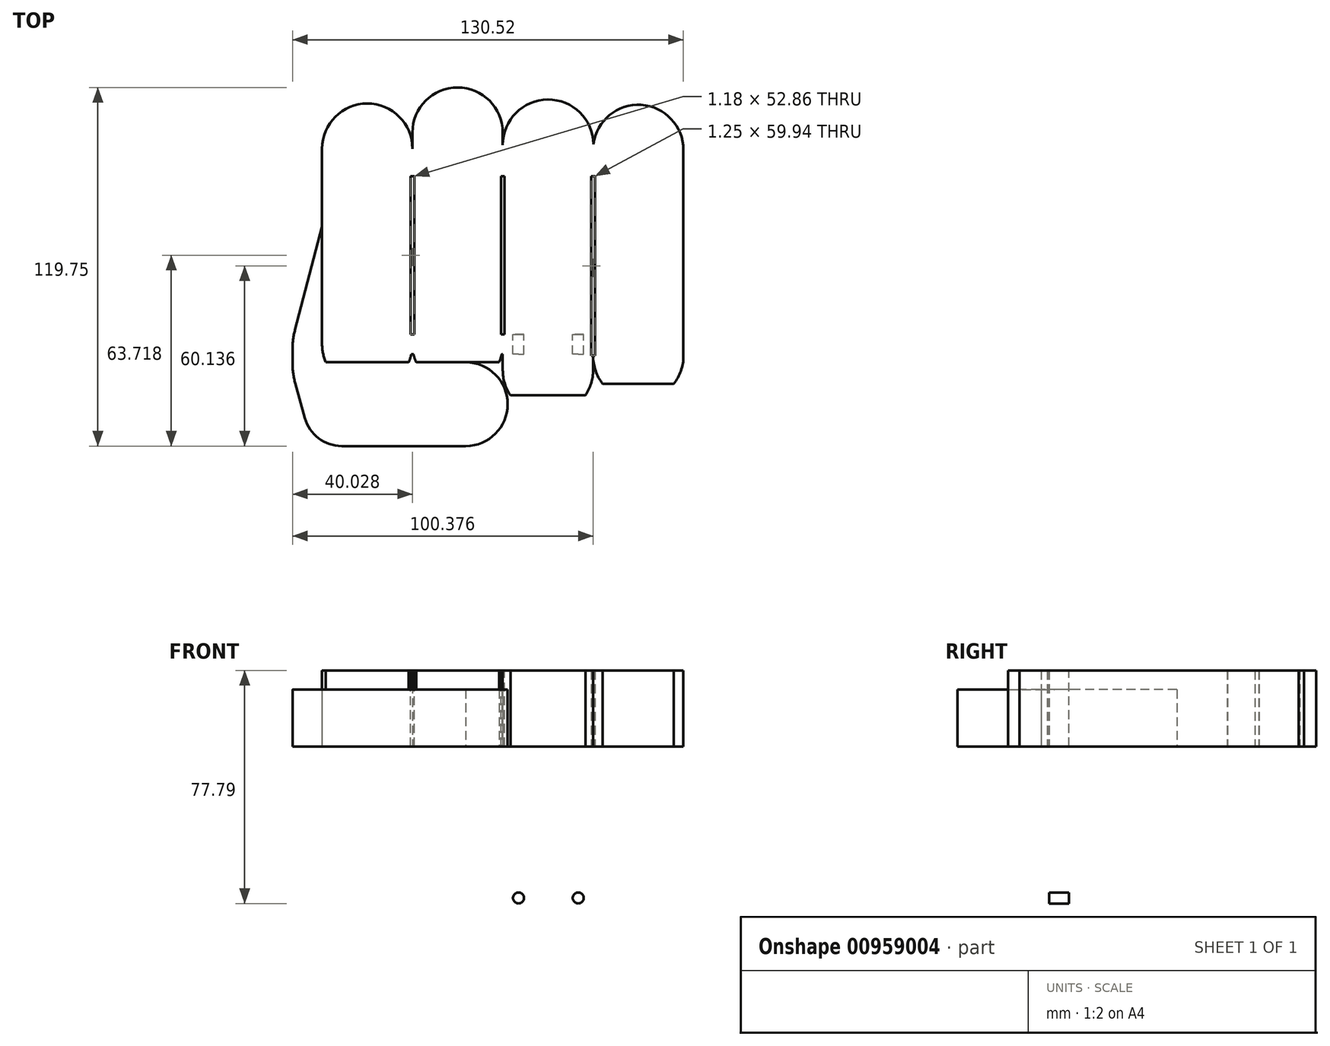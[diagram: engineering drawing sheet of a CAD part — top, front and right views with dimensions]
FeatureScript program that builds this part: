
annotation { "Feature Type Name" : "Feature", "Feature Type Description" : "" }
export const myFeature = defineFeature(function(context is Context, id is Id, definition is map)
    precondition{}
    {
        {
            var Q0;
            Q0=qCreatedBy(makeId("Top.planeOp"),FACE);
            var sketch = newSketch(context, id + "F0", { "sketchPlane" : qUnion([Q0])});
            skPoint(sketch, "E0.middle", {"position": v(0, 0) * mm});
            skArc(sketch, "E1", {"start": v(-30.16, -39.29) * mm, "mid": v(-29.85, -42.36) * mm, "end": v(-28.91, -45.3) * mm});
            skArc(sketch, "E2", {"start": v(0, -47.92) * mm, "mid": v(0.66, -52.32) * mm, "end": v(2.57, -56.34) * mm});
            skArc(sketch, "E3", {"start": v(-60.32, -39.28) * mm, "mid": v(-60, -42.35) * mm, "end": v(-59.07, -45.3) * mm});
            skArc(sketch, "E4", {"start": v(30.17, -43.19) * mm, "mid": v(31, -48.13) * mm, "end": v(33.4, -52.53) * mm});
            skLineSegment(sketch, "E5", {"start": v(-59.07, -45.3) * mm, "end": v(-31.41, -45.3) * mm});
            skArc(sketch, "E6.trimOffspring", {"start": v(-31.41, -45.3) * mm, "mid": v(-30.48, -42.36) * mm, "end": v(-30.16, -39.29) * mm});
            skArc(sketch, "E7.trimOffspring", {"start": v(-1.25, -45.3) * mm, "mid": v(-0.32, -42.36) * mm, "end": v(0, -39.29) * mm});
            skLineSegment(sketch, "E8.trimOffspring", {"start": v(-28.91, -45.3) * mm, "end": v(-1.25, -45.3) * mm});
            skArc(sketch, "E9", {"start": v(-12.33, -73.25) * mm, "mid": v(1.64, -59.27) * mm, "end": v(-12.33, -45.3) * mm});
            skLineSegment(sketch, "E10", {"start": v(-63.46, -73.25) * mm, "end": v(-12.33, -73.25) * mm});
            skLineSegment(sketch, "E11", {"start": v(33.4, -52.53) * mm, "end": v(57.09, -52.53) * mm});
            skArc(sketch, "E12.trimOffspring", {"start": v(27.6, -56.34) * mm, "mid": v(29.5, -52.32) * mm, "end": v(30.16, -47.92) * mm});
            skArc(sketch, "E13.trimOffspring", {"start": v(57.09, -52.53) * mm, "mid": v(59.5, -48.13) * mm, "end": v(60.33, -43.19) * mm});
            skArc(sketch, "E14", {"start": v(-30.16, 26.05) * mm, "mid": v(-45.24, 41.14) * mm, "end": v(-60.32, 26.05) * mm});
            skArc(sketch, "E15", {"start": v(0, 31.42) * mm, "mid": v(-15.08, 46.5) * mm, "end": v(-30.16, 31.42) * mm});
            skArc(sketch, "E16", {"start": v(60.33, 25.64) * mm, "mid": v(46.2, 40.7) * mm, "end": v(30.29, 27.55) * mm});
            skLineSegment(sketch, "E17", {"start": v(-60.32, 26.05) * mm, "end": v(-60.32, -39.28) * mm});
            skLineSegment(sketch, "E18", {"start": v(-30.16, 31.42) * mm, "end": v(-30.16, 26.05) * mm});
            skLineSegment(sketch, "E19", {"start": v(0, 31.42) * mm, "end": v(0, 27.33) * mm});
            skLineSegment(sketch, "E20", {"start": v(60.33, -43.19) * mm, "end": v(60.33, 25.64) * mm});
            skLineSegment(sketch, "E21", {"start": v(2.57, -56.34) * mm, "end": v(27.6, -56.34) * mm});
            skArc(sketch, "E22", {"start": v(30.29, 27.55) * mm, "mid": v(15.04, 42.47) * mm, "end": v(0, 27.33) * mm});
            skLineSegment(sketch, "E23", {"start": v(-63.46, -73.25) * mm, "end": v(-70.19, -49.07) * mm});
            skLineSegment(sketch, "E24", {"start": v(-70.19, -49.07) * mm, "end": v(-70.19, -37.56) * mm});
            skLineSegment(sketch, "E25.bottom", {"start": v(-29.57, 16.9) * mm, "end": v(-30.75, 16.9) * mm});
            skLineSegment(sketch, "E25.left", {"start": v(-29.57, 16.9) * mm, "end": v(-29.57, -38.59) * mm});
            skLineSegment(sketch, "E25.right", {"start": v(-30.75, 16.9) * mm, "end": v(-30.75, -38.59) * mm});
            skPoint(sketch, "E25.middle", {"position": v(-30.16, -11.2) * mm});
            skLineSegment(sketch, "E26.bottom", {"start": v(0.52, 16.88) * mm, "end": v(-0.52, 16.88) * mm});
            skLineSegment(sketch, "E26.left", {"start": v(0.52, 16.88) * mm, "end": v(0.52, -39) * mm});
            skLineSegment(sketch, "E26.right", {"start": v(-0.52, 16.88) * mm, "end": v(-0.52, -39) * mm});
            skPoint(sketch, "E26.middle", {"position": v(0, -11.2) * mm});
            skPoint(sketch, "E27.middle", {"position": v(30.18, -15.53) * mm});
            skLineSegment(sketch, "E28.bottom", {"start": v(30.81, 16.86) * mm, "end": v(29.56, 16.86) * mm});
            skLineSegment(sketch, "E28.left", {"start": v(30.81, 16.86) * mm, "end": v(30.81, -43.09) * mm});
            skLineSegment(sketch, "E28.right", {"start": v(29.56, 16.86) * mm, "end": v(29.56, -43.09) * mm});
            skPoint(sketch, "E28.middle", {"position": v(30.19, -13.17) * mm});
            skLineSegment(sketch, "E29", {"start": v(30.16, -47.92) * mm, "end": v(30.17, -43.19) * mm});
            skLineSegment(sketch, "E30", {"start": v(0, -47.92) * mm, "end": v(0, -39.29) * mm});
            skLineSegment(sketch, "E31", {"start": v(29.56, -43.09) * mm, "end": v(30.81, -43.09) * mm});
            skPoint(sketch, "E32.orphan", {"position": v(30.81, -43.19) * mm});
            skPoint(sketch, "E33.orphan", {"position": v(29.56, -43.19) * mm});
            skLineSegment(sketch, "E34", {"start": v(-0.52, -39) * mm, "end": v(0.52, -39) * mm});
            skPoint(sketch, "E35.orphan", {"position": v(0.52, -39.29) * mm});
            skPoint(sketch, "E36.orphan", {"position": v(-0.52, -39.29) * mm});
            skLineSegment(sketch, "E37", {"start": v(-60.32, 0) * mm, "end": v(-70.19, -37.56) * mm});
            skLineSegment(sketch, "E38", {"start": v(-30.75, -38.59) * mm, "end": v(-29.57, -38.59) * mm});
            skPoint(sketch, "E39.orphan", {"position": v(-29.57, -39.29) * mm});
            skPoint(sketch, "E40.orphan", {"position": v(-30.75, -39.29) * mm});
            skPoint(sketch, "E41.oppositeSnap0", {"position": v(-15.08, 46.5) * mm});
            skLineSegment(sketch, "E41.bottom", {"start": v(-70.19, -73.25) * mm, "end": v(60.33, -73.25) * mm, "construction": true});
            skLineSegment(sketch, "E41.top", {"start": v(-70.19, 46.5) * mm, "end": v(60.33, 46.5) * mm, "construction": true});
            skLineSegment(sketch, "E41.left", {"start": v(-70.19, -73.25) * mm, "end": v(-70.19, 46.5) * mm, "construction": true});
            skLineSegment(sketch, "E41.right", {"start": v(60.33, -73.25) * mm, "end": v(60.33, 46.5) * mm, "construction": true});
            skLineSegment(sketch, "E42", {"start": v(60.33, 46.5) * mm, "end": v(-70.19, -73.25) * mm, "construction": true});
            skLineSegment(sketch, "E43", {"start": v(-70.19, 46.5) * mm, "end": v(60.33, -73.25) * mm, "construction": true});
            skPoint(sketch, "E44", {"position": v(-4.93, -13.37) * mm});
            skSolve(sketch);
        }
        {
            var Q0;
            {var subQ4=sQuery(id+"F0.wireOp",EDGE,"E1");Q0=makeQuery(id+"F0.imprint","IMPRINT",FACE,{"disambiguationData":[TD([[makeQuery(id+"F0.imprint","IMPRINT",EDGE,{"derivedFrom":subQ4}),1.0]])]});}
            extrude(context, id + "F1", {"entities" : qUnion([Q0]), "depth" : 25.4 * mm, "offsetDistance" : 25.4 * mm});
        }
        {
            var Q0;
            {var subQ5=sQuery(id+"F0.wireOp",EDGE,"E1");Q0=makeQuery(id+"F0.imprint","IMPRINT",FACE,{"disambiguationData":[TD([[makeQuery(id+"F0.imprint","IMPRINT",EDGE,{"derivedFrom":subQ5}),-1.0]])]});}
            extrude(context, id + "F2", {"entities" : qUnion([Q0]), "operationType" : NewBodyOperationType.ADD, "depth" : 19.05 * mm, "offsetDistance" : 25.4 * mm});
        }
        {
            var Q0;
            {var subQ4=sQuery(id+"F0.wireOp",EDGE,"E1");Q0=makeQuery(id+"F0.imprint","IMPRINT",FACE,{"disambiguationData":[TD([[makeQuery(id+"F0.imprint","IMPRINT",EDGE,{"derivedFrom":subQ4}),1.0]])]});}
            var sketch = newSketch(context, id + "F3", { "sketchPlane" : qUnion([Q0])});
            skLineSegment(sketch, "E45.bottom", {"start": v(-70.2, 46.56) * mm, "end": v(60.33, 46.56) * mm, "construction": true});
            skLineSegment(sketch, "E45.top", {"start": v(-70.2, -73.3) * mm, "end": v(60.33, -73.3) * mm, "construction": true});
            skLineSegment(sketch, "E45.left", {"start": v(-70.2, 46.56) * mm, "end": v(-70.2, -73.3) * mm, "construction": true});
            skLineSegment(sketch, "E45.right", {"start": v(60.33, 46.56) * mm, "end": v(60.33, -73.3) * mm, "construction": true});
            skPoint(sketch, "E45.middle", {"position": v(-4.93, -13.37) * mm});
            skLineSegment(sketch, "E46", {"start": v(-70.2, 46.56) * mm, "end": v(60.33, -73.3) * mm, "construction": true});
            skLineSegment(sketch, "E47", {"start": v(-70.2, -73.3) * mm, "end": v(60.33, 46.56) * mm, "construction": true});
            skLineSegment(sketch, "E48", {"start": v(-4.93, -13.37) * mm, "end": v(-4.93, -73.3) * mm, "construction": true});
            skLineSegment(sketch, "E49.bottom", {"start": v(-39.33, -35.96) * mm, "end": v(29.46, -35.96) * mm});
            skLineSegment(sketch, "E49.top", {"start": v(-39.33, -42.6) * mm, "end": v(29.46, -42.6) * mm});
            skLineSegment(sketch, "E49.left", {"start": v(-39.33, -35.96) * mm, "end": v(-39.33, -42.6) * mm});
            skLineSegment(sketch, "E49.right", {"start": v(29.46, -35.96) * mm, "end": v(29.46, -42.6) * mm});
            skPoint(sketch, "E49.middle", {"position": v(-4.93, -39.28) * mm});
            skSolve(sketch);
        }
        {
            var Q0;
            Q0=makeQuery(id+"F2.opExtrude","SWEPT_EDGE",EDGE,{"disambiguationData":[OSD([sQuery(id+"F0.wireOp",EDGE,"E24"),sQuery(id+"F0.wireOp",EDGE,"E37")])]});
            var Q1;
            Q1=makeQuery(id+"F2.opExtrude","SWEPT_EDGE",EDGE,{"disambiguationData":[OSD([sQuery(id+"F0.wireOp",EDGE,"E23"),sQuery(id+"F0.wireOp",EDGE,"E24")])]});
            fillet(context, id + "F4", {"entities" : qUnion([Q0, Q1]), "radius" : 25.4 * mm, "tangentPropagation" : true, "allowEdgeOverflow" : false});
        }
        {
            var Q0;
            Q0=makeQuery(id+"F2.opExtrude","SWEPT_EDGE",EDGE,{"disambiguationData":[OSD([sQuery(id+"F0.wireOp",EDGE,"E10"),sQuery(id+"F0.wireOp",EDGE,"E23")])]});
            fillet(context, id + "F5", {"entities" : qUnion([Q0]), "radius" : 12.7 * mm, "tangentPropagation" : true, "allowEdgeOverflow" : false});
        }
        {
            var Q0;
            {var subQ1=sQuery(id+"F3.wireOp",EDGE,"E49.left");Q0=makeQuery(id+"F3.imprint","IMPRINT",FACE,{"disambiguationData":[TD([[makeQuery(id+"F3.imprint","IMPRINT",EDGE,{"derivedFrom":subQ1}),1.0]])]});}
            extrude(context, id + "F6", {"entities" : qUnion([Q0]), "operationType" : NewBodyOperationType.ADD, "oppositeDirection" : true, "depth" : 61.62 * mm, "offsetDistance" : 25.4 * mm});
        }
        {
            var Q0;
            Q0=makeQuery(id+"F6.opExtrude","SWEPT_FACE",FACE,{"disambiguationData":[OSD([sQuery(id+"F3.wireOp",EDGE,"E49.left")])]});
            extrude(context, id + "F7", {"entities" : qUnion([Q0]), "operationType" : NewBodyOperationType.ADD, "oppositeDirection" : true, "depth" : 45.47 * mm, "offsetDistance" : 25.4 * mm});
        }
        {
            var Q0;
            {var subQ0=sQuery(id+"F3.wireOp",EDGE,"E49.left");Q0=makeQuery(id+"F7.boolean.opBoolean","MERGE",FACE,{"derivedFrom":[makeQuery(id+"F6.opExtrude","CAP_FACE",FACE,{"disambiguationData":[OSD([sQuery(id+"F0.wireOp",EDGE,"E1"),sQuery(id+"F0.wireOp",EDGE,"E6.trimOffspring"),sQuery(id+"F0.wireOp",EDGE,"E7.trimOffspring"),sQuery(id+"F0.wireOp",EDGE,"E25.left"),sQuery(id+"F0.wireOp",EDGE,"E25.right"),sQuery(id+"F0.wireOp",EDGE,"E26.left"),sQuery(id+"F0.wireOp",EDGE,"E26.right"),sQuery(id+"F0.wireOp",EDGE,"E30"),sQuery(id+"F0.wireOp",EDGE,"E34"),sQuery(id+"F0.wireOp",EDGE,"E38"),sQuery(id+"F3.wireOp",EDGE,"E49.bottom"),sQuery(id+"F3.wireOp",EDGE,"E49.top"),subQ0,sQuery(id+"F3.wireOp",EDGE,"E49.right")])],"isStart":false}),makeQuery(id+"F7.opExtrude","SWEPT_FACE",FACE,{"disambiguationData":[OSD([subQ0]),TDD([makeQuery(id+"F6.opExtrude","CAP_EDGE",EDGE,{"disambiguationData":[OSD([subQ0])],"isStart":false})])]})]});}
            var Q1;
            Q1=makeQuery(id+"F1.opExtrude","CAP_FACE",FACE,{"disambiguationData":[OSD([sQuery(id+"F0.wireOp",EDGE,"E1"),sQuery(id+"F0.wireOp",EDGE,"E2"),sQuery(id+"F0.wireOp",EDGE,"E3"),sQuery(id+"F0.wireOp",EDGE,"E4"),sQuery(id+"F0.wireOp",EDGE,"E5"),sQuery(id+"F0.wireOp",EDGE,"E6.trimOffspring"),sQuery(id+"F0.wireOp",EDGE,"E7.trimOffspring"),sQuery(id+"F0.wireOp",EDGE,"E8.trimOffspring"),sQuery(id+"F0.wireOp",EDGE,"E11"),sQuery(id+"F0.wireOp",EDGE,"E12.trimOffspring"),sQuery(id+"F0.wireOp",EDGE,"E13.trimOffspring"),sQuery(id+"F0.wireOp",EDGE,"E14"),sQuery(id+"F0.wireOp",EDGE,"E15"),sQuery(id+"F0.wireOp",EDGE,"E16"),sQuery(id+"F0.wireOp",EDGE,"E17"),sQuery(id+"F0.wireOp",EDGE,"E18"),sQuery(id+"F0.wireOp",EDGE,"E19"),sQuery(id+"F0.wireOp",EDGE,"E20"),sQuery(id+"F0.wireOp",EDGE,"E21"),sQuery(id+"F0.wireOp",EDGE,"E22"),sQuery(id+"F0.wireOp",EDGE,"E25.bottom"),sQuery(id+"F0.wireOp",EDGE,"E25.left"),sQuery(id+"F0.wireOp",EDGE,"E25.right"),sQuery(id+"F0.wireOp",EDGE,"E26.bottom"),sQuery(id+"F0.wireOp",EDGE,"E26.left"),sQuery(id+"F0.wireOp",EDGE,"E26.right"),sQuery(id+"F0.wireOp",EDGE,"E28.bottom"),sQuery(id+"F0.wireOp",EDGE,"E28.left"),sQuery(id+"F0.wireOp",EDGE,"E28.right"),sQuery(id+"F0.wireOp",EDGE,"E29"),sQuery(id+"F0.wireOp",EDGE,"E30"),sQuery(id+"F0.wireOp",EDGE,"E31"),sQuery(id+"F0.wireOp",EDGE,"E34"),sQuery(id+"F0.wireOp",EDGE,"E38")])],"isStart":false});
            extrude(context, id + "F8", {"entities" : qUnion([Q0]), "operationType" : NewBodyOperationType.ADD, "endBound" : BoundingType.UP_TO_SURFACE, "oppositeDirection" : true, "depth" : 25.4 * mm, "endBoundEntityFace" : qUnion([Q1]), "offsetDistance" : 25.4 * mm});
        }
        {
            var Q0;
            {var subQ0=sQuery(id+"F3.wireOp",EDGE,"E49.left");var subQ1=sQuery(id+"F3.wireOp",EDGE,"E49.bottom");Q0=makeQuery(id+"F8.boolean.opBoolean","MERGE",FACE,{"derivedFrom":[makeQuery(id+"F7.boolean.opBoolean","MERGE",FACE,{"derivedFrom":[makeQuery(id+"F6.opExtrude","SWEPT_FACE",FACE,{"disambiguationData":[OSD([subQ1]),TDD([makeQuery(id+"F3.imprint","IMPRINT",EDGE,{"disambiguationData":[TD([[makeQuery(id+"F3.imprint","INTERSECT",VERTEX,{"derivedFrom":[subQ1,subQ0]}),-1.0]])],"derivedFrom":subQ1})])]}),makeQuery(id+"F6.opExtrude","SWEPT_FACE",FACE,{"disambiguationData":[OSD([subQ1]),TDD([makeQuery(id+"F3.imprint","IMPRINT",EDGE,{"disambiguationData":[TD([[makeQuery(id+"F3.imprint","INTERSECT",VERTEX,{"derivedFrom":[makeQuery(id+"F0.imprint","IMPRINT",EDGE,{"derivedFrom":sQuery(id+"F0.wireOp",EDGE,"E25.left")}),subQ1]}),-1.0]])],"derivedFrom":subQ1})])]}),makeQuery(id+"F6.opExtrude","SWEPT_FACE",FACE,{"disambiguationData":[OSD([subQ1]),TDD([makeQuery(id+"F3.imprint","IMPRINT",EDGE,{"disambiguationData":[TD([[makeQuery(id+"F3.imprint","INTERSECT",VERTEX,{"derivedFrom":[subQ1,sQuery(id+"F3.wireOp",EDGE,"E49.right")]}),1.0]])],"derivedFrom":subQ1})])]}),makeQuery(id+"F7.opExtrude","SWEPT_FACE",FACE,{"disambiguationData":[OSD([subQ1,subQ0])]})]}),makeQuery(id+"F8.opExtrude","SWEPT_FACE",FACE,{"disambiguationData":[OSD([subQ1,subQ0])]})]});}
            var sketch = newSketch(context, id + "F9", { "sketchPlane" : qUnion([Q0])});
            skLineSegment(sketch, "E50.bottom", {"start": v(39.33, 0) * mm, "end": v(-29.46, 0) * mm});
            skLineSegment(sketch, "E50.top", {"start": v(39.33, -61.62) * mm, "end": v(-29.46, -61.62) * mm});
            skLineSegment(sketch, "E50.left", {"start": v(39.33, 0) * mm, "end": v(39.33, -61.62) * mm});
            skLineSegment(sketch, "E50.right", {"start": v(-29.46, 0) * mm, "end": v(-29.46, -61.62) * mm});
            skPoint(sketch, "E50.middle", {"position": v(4.93, -30.81) * mm});
            skPoint(sketch, "E50.middle.positionSnap0", {"position": v(39.33, -30.81) * mm});
            skPoint(sketch, "E50.middle.positionSnap1", {"position": v(4.93, -61.62) * mm});
            skPoint(sketch, "E50.centerSnap0", {"position": v(39.33, -30.81) * mm});
            skPoint(sketch, "E50.centerSnap1", {"position": v(4.93, -61.62) * mm});
            skLineSegment(sketch, "E51", {"start": v(-29.46, -50.55) * mm, "end": v(39.33, -50.55) * mm});
            skCircle(sketch, "E52", {"center": v(-25.2, -50.55) * mm, "radius": 1.84 * mm});
            skCircle(sketch, "E53", {"center": v(-5.26, -50.55) * mm, "radius": 1.84 * mm});
            skCircle(sketch, "E54", {"center": v(15.13, -50.55) * mm, "radius": 1.84 * mm});
            skCircle(sketch, "E55", {"center": v(35.07, -50.55) * mm, "radius": 1.84 * mm});
            skSolve(sketch);
        }
        {
            var Q0;
            {var subQ0=sQuery(id+"F9.wireOp",EDGE,"E52");var subQ1=sQuery(id+"F9.wireOp",EDGE,"E51");var subQ2=makeQuery(id+"F9.imprint","INTERSECT",VERTEX,{"disambiguationData":[OD(0.0)],"derivedFrom":[subQ1,subQ0]});Q0=makeQuery(id+"F9.imprint","IMPRINT",FACE,{"disambiguationData":[TD([[makeQuery(id+"F9.imprint","IMPRINT",EDGE,{"disambiguationData":[TD([[subQ2,-1.0]])],"derivedFrom":subQ1}),1.0]])]});}
            var Q1;
            {var subQ0=sQuery(id+"F9.wireOp",EDGE,"E52");var subQ1=sQuery(id+"F9.wireOp",EDGE,"E51");var subQ2=makeQuery(id+"F9.imprint","INTERSECT",VERTEX,{"disambiguationData":[OD(0.0)],"derivedFrom":[subQ1,subQ0]});Q1=makeQuery(id+"F9.imprint","IMPRINT",FACE,{"disambiguationData":[TD([[makeQuery(id+"F9.imprint","IMPRINT",EDGE,{"disambiguationData":[TD([[subQ2,-1.0]])],"derivedFrom":subQ1}),-1.0]])]});}
            var Q2;
            {var subQ0=sQuery(id+"F9.wireOp",EDGE,"E53");var subQ1=sQuery(id+"F9.wireOp",EDGE,"E51");var subQ2=makeQuery(id+"F9.imprint","INTERSECT",VERTEX,{"disambiguationData":[OD(0.0)],"derivedFrom":[subQ1,subQ0]});Q2=makeQuery(id+"F9.imprint","IMPRINT",FACE,{"disambiguationData":[TD([[makeQuery(id+"F9.imprint","IMPRINT",EDGE,{"disambiguationData":[TD([[subQ2,-1.0]])],"derivedFrom":subQ1}),1.0]])]});}
            var Q3;
            {var subQ0=sQuery(id+"F9.wireOp",EDGE,"E53");var subQ1=sQuery(id+"F9.wireOp",EDGE,"E51");var subQ2=makeQuery(id+"F9.imprint","INTERSECT",VERTEX,{"disambiguationData":[OD(0.0)],"derivedFrom":[subQ1,subQ0]});Q3=makeQuery(id+"F9.imprint","IMPRINT",FACE,{"disambiguationData":[TD([[makeQuery(id+"F9.imprint","IMPRINT",EDGE,{"disambiguationData":[TD([[subQ2,-1.0]])],"derivedFrom":subQ1}),-1.0]])]});}
            var Q4;
            {var subQ0=sQuery(id+"F9.wireOp",EDGE,"E54");var subQ1=sQuery(id+"F9.wireOp",EDGE,"E51");var subQ2=makeQuery(id+"F9.imprint","INTERSECT",VERTEX,{"disambiguationData":[OD(0.0)],"derivedFrom":[subQ1,subQ0]});Q4=makeQuery(id+"F9.imprint","IMPRINT",FACE,{"disambiguationData":[TD([[makeQuery(id+"F9.imprint","IMPRINT",EDGE,{"disambiguationData":[TD([[subQ2,-1.0]])],"derivedFrom":subQ1}),1.0]])]});}
            var Q5;
            {var subQ0=sQuery(id+"F9.wireOp",EDGE,"E54");var subQ1=sQuery(id+"F9.wireOp",EDGE,"E51");var subQ2=makeQuery(id+"F9.imprint","INTERSECT",VERTEX,{"disambiguationData":[OD(0.0)],"derivedFrom":[subQ1,subQ0]});Q5=makeQuery(id+"F9.imprint","IMPRINT",FACE,{"disambiguationData":[TD([[makeQuery(id+"F9.imprint","IMPRINT",EDGE,{"disambiguationData":[TD([[subQ2,-1.0]])],"derivedFrom":subQ1}),-1.0]])]});}
            var Q6;
            {var subQ0=sQuery(id+"F9.wireOp",EDGE,"E55");var subQ1=sQuery(id+"F9.wireOp",EDGE,"E51");var subQ2=makeQuery(id+"F9.imprint","INTERSECT",VERTEX,{"disambiguationData":[OD(0.0)],"derivedFrom":[subQ1,subQ0]});Q6=makeQuery(id+"F9.imprint","IMPRINT",FACE,{"disambiguationData":[TD([[makeQuery(id+"F9.imprint","IMPRINT",EDGE,{"disambiguationData":[TD([[subQ2,-1.0]])],"derivedFrom":subQ1}),1.0]])]});}
            var Q7;
            {var subQ0=sQuery(id+"F9.wireOp",EDGE,"E55");var subQ1=sQuery(id+"F9.wireOp",EDGE,"E51");var subQ2=makeQuery(id+"F9.imprint","INTERSECT",VERTEX,{"disambiguationData":[OD(0.0)],"derivedFrom":[subQ1,subQ0]});Q7=makeQuery(id+"F9.imprint","IMPRINT",FACE,{"disambiguationData":[TD([[makeQuery(id+"F9.imprint","IMPRINT",EDGE,{"disambiguationData":[TD([[subQ2,-1.0]])],"derivedFrom":subQ1}),-1.0]])]});}
            extrude(context, id + "F10", {"entities" : qUnion([Q0, Q1, Q2, Q3, Q4, Q5, Q6, Q7]), "operationType" : NewBodyOperationType.REMOVE, "endBound" : BoundingType.THROUGH_ALL, "oppositeDirection" : true, "depth" : 25.4 * mm, "offsetDistance" : 25.4 * mm});
        }
    });
